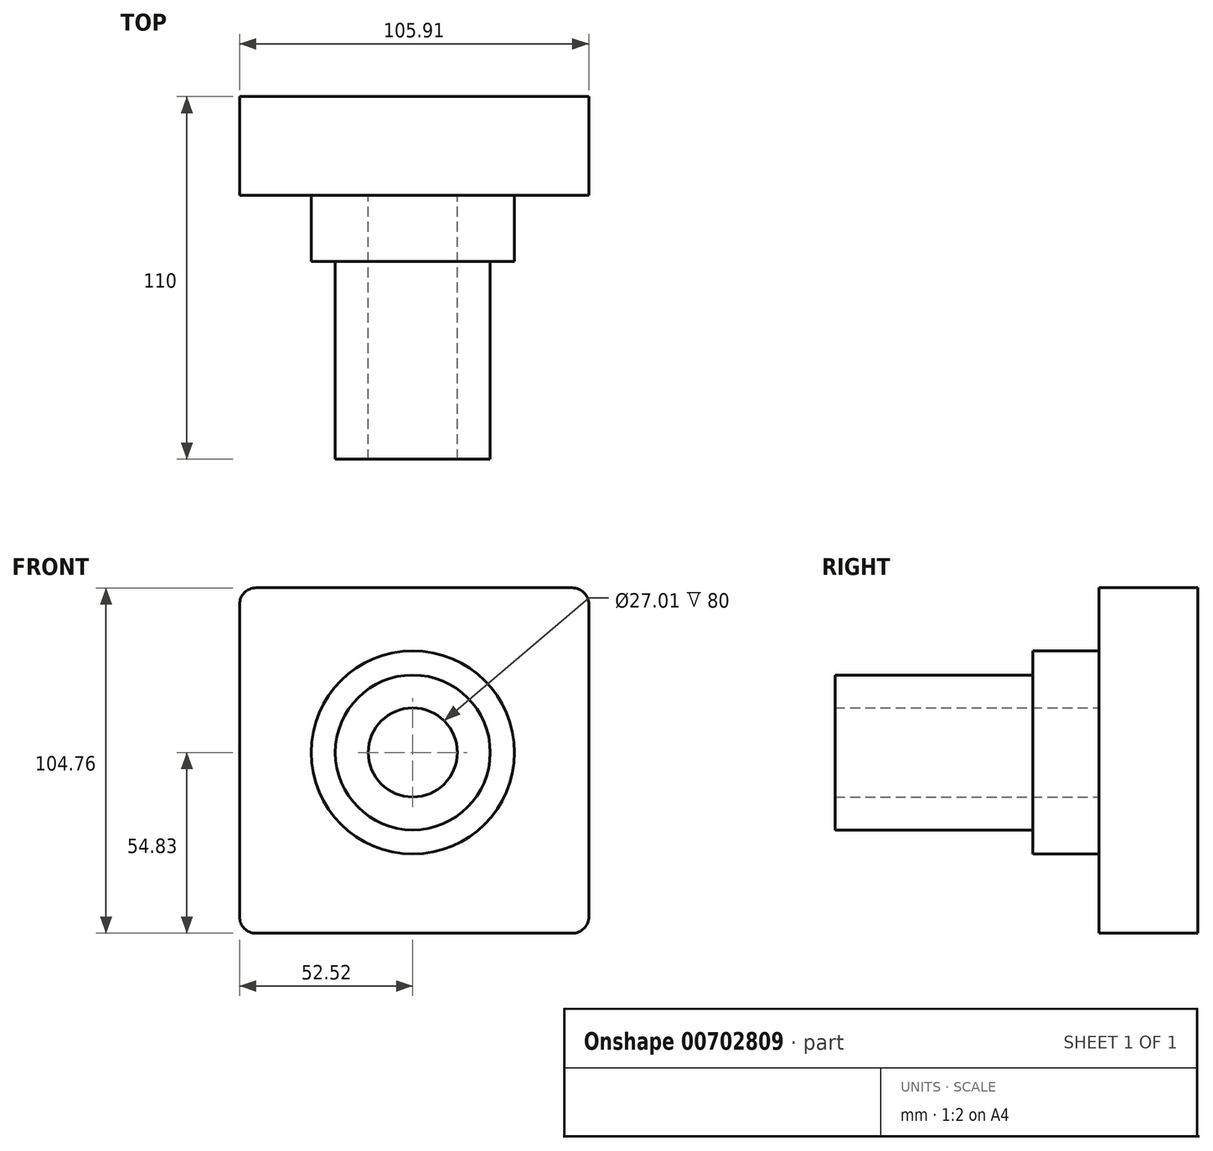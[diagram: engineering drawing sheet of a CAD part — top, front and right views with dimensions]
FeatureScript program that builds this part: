
annotation { "Feature Type Name" : "Feature", "Feature Type Description" : "" }
export const myFeature = defineFeature(function(context is Context, id is Id, definition is map)
    precondition{}
    {
        {
            var Q0;
            Q0=qCreatedBy(makeId("Front.planeOp"),FACE);
            var sketch = newSketch(context, id + "F0", { "sketchPlane" : qUnion([Q0])});
            skLineSegment(sketch, "E0", {"start": v(53.39, 49.93) * mm, "end": v(53.39, -54.83) * mm});
            skLineSegment(sketch, "E1", {"start": v(53.39, -54.83) * mm, "end": v(-52.52, -54.83) * mm});
            skLineSegment(sketch, "E2", {"start": v(-52.52, -54.83) * mm, "end": v(-52.52, 49.93) * mm});
            skPoint(sketch, "E3.start.orphan", {"position": v(-57.42, 49.93) * mm});
            skLineSegment(sketch, "E4", {"start": v(-52.52, 49.93) * mm, "end": v(53.39, 49.93) * mm});
            skSolve(sketch);
        }
        {
            var Q0;
            Q0 = qSketchRegion(id + "F0", true);
            extrude(context, id + "F1", {"entities" : qUnion([Q0]), "depth" : 30 * mm, "offsetDistance" : 25.4 * mm});
        }
        {
            var Q0;
            Q0=makeQuery(id+"F1.opExtrude","SWEPT_EDGE",EDGE,{"disambiguationData":[OSD([sQuery(id+"F0.wireOp",EDGE,"E0"),sQuery(id+"F0.wireOp",EDGE,"E4")])]});
            var Q1;
            Q1=makeQuery(id+"F1.opExtrude","SWEPT_EDGE",EDGE,{"disambiguationData":[OSD([sQuery(id+"F0.wireOp",EDGE,"E0"),sQuery(id+"F0.wireOp",EDGE,"E1")])]});
            var Q2;
            Q2=makeQuery(id+"F1.opExtrude","SWEPT_EDGE",EDGE,{"disambiguationData":[OSD([sQuery(id+"F0.wireOp",EDGE,"E2"),sQuery(id+"F0.wireOp",EDGE,"E4")])]});
            var Q3;
            Q3=makeQuery(id+"F1.opExtrude","SWEPT_EDGE",EDGE,{"disambiguationData":[OSD([sQuery(id+"F0.wireOp",EDGE,"E1"),sQuery(id+"F0.wireOp",EDGE,"E2")])]});
            fillet(context, id + "F2", {"entities" : qUnion([Q0, Q1, Q2, Q3]), "radius" : 5 * mm, "tangentPropagation" : true, "allowEdgeOverflow" : false});
        }
        {
            var Q0;
            Q0=makeQuery(id+"F1.opExtrude","CAP_FACE",FACE,{"disambiguationData":[OSD([sQuery(id+"F0.wireOp",EDGE,"E0"),sQuery(id+"F0.wireOp",EDGE,"E1"),sQuery(id+"F0.wireOp",EDGE,"E2"),sQuery(id+"F0.wireOp",EDGE,"E4")])],"isStart":false});
            var sketch = newSketch(context, id + "F3", { "sketchPlane" : qUnion([Q0])});
            skCircle(sketch, "E5", {"center": v(0, 0) * mm, "radius": 30.81 * mm});
            skCircle(sketch, "E6", {"center": v(0, 0) * mm, "radius": 23.38 * mm});
            skSolve(sketch);
        }
        {
            var Q0;
            Q0 = qSketchRegion(id + "F3", true);
            extrude(context, id + "F4", {"entities" : qUnion([Q0]), "operationType" : NewBodyOperationType.ADD, "depth" : 20 * mm, "offsetDistance" : 25 * mm});
        }
        {
            var Q0;
            Q0=makeQuery(id+"F4.boolean.opBoolean","SPLIT",FACE,{"disambiguationData":[TD([makeQuery(id+"F4.opExtrude","SWEPT_FACE",FACE,{"disambiguationData":[OSD([sQuery(id+"F3.wireOp",EDGE,"E6")])]})])],"derivedFrom":makeQuery(id+"F1.opExtrude","CAP_FACE",FACE,{"disambiguationData":[OSD([sQuery(id+"F0.wireOp",EDGE,"E0"),sQuery(id+"F0.wireOp",EDGE,"E1"),sQuery(id+"F0.wireOp",EDGE,"E2"),sQuery(id+"F0.wireOp",EDGE,"E4")])],"isStart":false})});
            var sketch = newSketch(context, id + "F5", { "sketchPlane" : qUnion([Q0])});
            skCircle(sketch, "E7", {"center": v(0, 0) * mm, "radius": 23.5 * mm});
            skCircle(sketch, "E8", {"center": v(0, 0) * mm, "radius": 13.5 * mm});
            skSolve(sketch);
        }
        {
            var Q0;
            Q0 = qSketchRegion(id + "F5", true);
            extrude(context, id + "F6", {"entities" : qUnion([Q0]), "operationType" : NewBodyOperationType.ADD, "depth" : 80 * mm, "offsetDistance" : 25 * mm});
        }
    });
